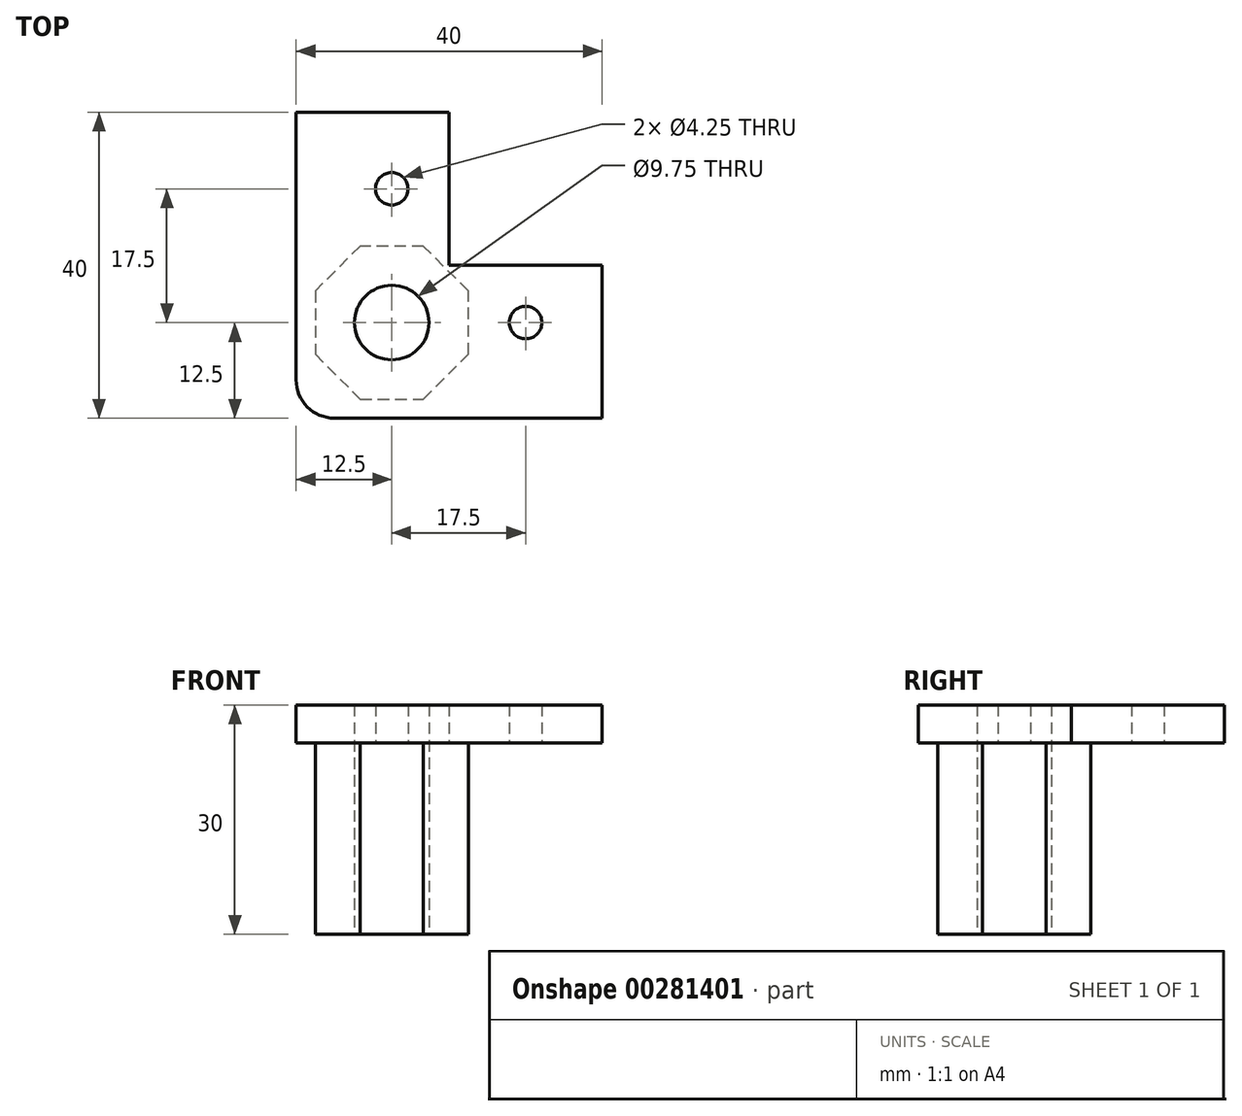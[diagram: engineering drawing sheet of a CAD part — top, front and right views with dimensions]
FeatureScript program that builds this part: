
annotation { "Feature Type Name" : "Feature", "Feature Type Description" : "" }
export const myFeature = defineFeature(function(context is Context, id is Id, definition is map)
    precondition{}
    {
        {
            var Q0;
            Q0=qCreatedBy(makeId("Top.planeOp"),FACE);
            var sketch = newSketch(context, id + "F0", { "sketchPlane" : qUnion([Q0])});
            skCircle(sketch, "E0", {"center": v(0, 0) * mm, "radius": 4.88 * mm});
            skLineSegment(sketch, "E1", {"start": v(-12.5, 0) * mm, "end": v(-12.5, 27.5) * mm});
            skLineSegment(sketch, "E2", {"start": v(-12.5, 27.5) * mm, "end": v(7.5, 27.5) * mm});
            skLineSegment(sketch, "E3", {"start": v(7.5, 27.5) * mm, "end": v(7.5, 7.5) * mm});
            skLineSegment(sketch, "E4", {"start": v(7.5, 7.5) * mm, "end": v(27.5, 7.5) * mm});
            skLineSegment(sketch, "E5", {"start": v(27.5, 7.5) * mm, "end": v(27.5, -12.5) * mm});
            skLineSegment(sketch, "E6", {"start": v(27.5, -12.5) * mm, "end": v(-7.5, -12.5) * mm});
            skLineSegment(sketch, "E7", {"start": v(-12.5, -7.5) * mm, "end": v(-12.5, 0) * mm});
            skCircle(sketch, "E8", {"center": v(0, 17.5) * mm, "radius": 2.12 * mm});
            skCircle(sketch, "E9", {"center": v(17.5, 0) * mm, "radius": 2.12 * mm});
            skPoint(sketch, "E10.visualSharp", {"position": v(-12.5, -12.5) * mm});
            skLineSegment(sketch, "E10.filletArc", {"start": v(-12.5, -12.5) * mm, "end": v(-12.5, -12.5) * mm});
            skArc(sketch, "E11.filletArc", {"start": v(-12.5, -7.5) * mm, "mid": v(-11.04, -11.04) * mm, "end": v(-7.5, -12.5) * mm});
            skSolve(sketch);
        }
        {
            var Q0;
            Q0=qSketchRegion(id+"F0",true);
            extrude(context, id + "F1", {"entities" : qUnion([Q0]), "depth" : 5 * mm});
        }
        {
            var Q0;
            Q0=makeQuery(id+"F1.opExtrude","CAP_FACE",FACE,{"disambiguationData":[OSD([sQuery(id+"F0.wireOp",EDGE,"E0"),sQuery(id+"F0.wireOp",EDGE,"E1"),sQuery(id+"F0.wireOp",EDGE,"E2"),sQuery(id+"F0.wireOp",EDGE,"E3"),sQuery(id+"F0.wireOp",EDGE,"E4"),sQuery(id+"F0.wireOp",EDGE,"E5"),sQuery(id+"F0.wireOp",EDGE,"E6"),sQuery(id+"F0.wireOp",EDGE,"E7"),sQuery(id+"F0.wireOp",EDGE,"E8"),sQuery(id+"F0.wireOp",EDGE,"E9"),sQuery(id+"F0.wireOp",EDGE,"E10.filletArc")])],"isStart":true});
            var sketch = newSketch(context, id + "F2", { "sketchPlane" : qUnion([Q0])});
            skCircle(sketch, "E12.cCircle", {"center": v(0, 0) * mm, "radius": 10 * mm, "construction": true});
            skLineSegment(sketch, "E12.0", {"start": v(10, 4.14) * mm, "end": v(10, -4.14) * mm});
            skLineSegment(sketch, "E12.1", {"start": v(10, -4.14) * mm, "end": v(4.14, -10) * mm});
            skLineSegment(sketch, "E12.2", {"start": v(4.14, -10) * mm, "end": v(-4.14, -10) * mm});
            skLineSegment(sketch, "E12.3", {"start": v(-4.14, -10) * mm, "end": v(-10, -4.14) * mm});
            skLineSegment(sketch, "E12.4", {"start": v(-10, -4.14) * mm, "end": v(-10, 4.14) * mm});
            skLineSegment(sketch, "E12.5", {"start": v(-10, 4.14) * mm, "end": v(-4.14, 10) * mm});
            skLineSegment(sketch, "E12.6", {"start": v(-4.14, 10) * mm, "end": v(4.14, 10) * mm});
            skLineSegment(sketch, "E12.7", {"start": v(4.14, 10) * mm, "end": v(10, 4.14) * mm});
            skPoint(sketch, "E12.0.midPoint", {"position": v(10, 0) * mm});
            skCircle(sketch, "E13", {"center": v(0, 0) * mm, "radius": 4.88 * mm});
            skSolve(sketch);
        }
        {
            var Q0;
            Q0=qSketchRegion(id+"F2",true);
            extrude(context, id + "F3", {"entities" : qUnion([Q0]), "operationType" : NewBodyOperationType.ADD, "depth" : 25 * mm});
        }
    });
